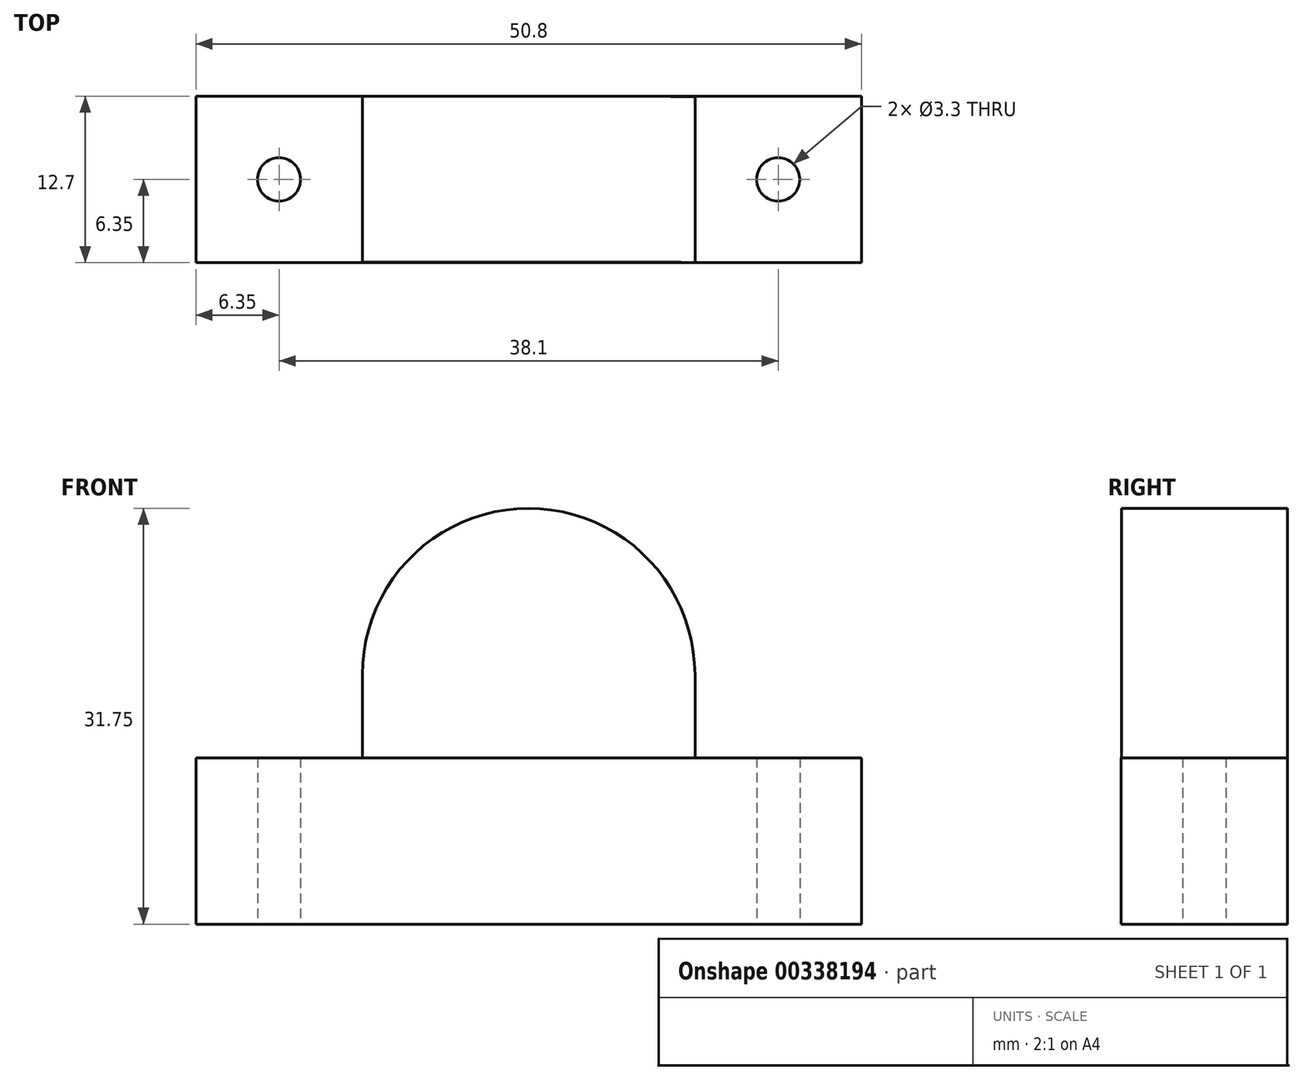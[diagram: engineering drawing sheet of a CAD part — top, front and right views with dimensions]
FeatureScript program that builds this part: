
annotation { "Feature Type Name" : "Feature", "Feature Type Description" : "" }
export const myFeature = defineFeature(function(context is Context, id is Id, definition is map)
    precondition{}
    {
        {
            var Q0;
            Q0=qCreatedBy(makeId("Top.planeOp"),FACE);
            var sketch = newSketch(context, id + "F0", { "sketchPlane" : qUnion([Q0])});
            skLineSegment(sketch, "E0.bottom", {"start": v(25.4, -6.35) * mm, "end": v(-25.4, -6.35) * mm});
            skLineSegment(sketch, "E0.top", {"start": v(25.4, 6.35) * mm, "end": v(-25.4, 6.35) * mm});
            skLineSegment(sketch, "E0.left", {"start": v(25.4, -6.35) * mm, "end": v(25.4, 6.35) * mm});
            skLineSegment(sketch, "E0.right", {"start": v(-25.4, -6.35) * mm, "end": v(-25.4, 6.35) * mm});
            skPoint(sketch, "E0.middle", {"position": v(0, 0) * mm});
            skCircle(sketch, "E1", {"center": v(19.05, 0) * mm, "radius": 1.65 * mm});
            skCircle(sketch, "E2", {"center": v(-19.05, 0) * mm, "radius": 1.65 * mm});
            skSolve(sketch);
        }
        {
            var Q0;
            Q0=makeQuery(id+"F0.imprint","IMPRINT",FACE,{"disambiguationData":[TD([[makeQuery(id+"F0.imprint","IMPRINT",EDGE,{"derivedFrom":sQuery(id+"F0.wireOp",EDGE,"E0.bottom")}),-1.0]])]});
            var sketch = newSketch(context, id + "F1", { "sketchPlane" : qUnion([Q0])});
            skLineSegment(sketch, "E3", {"start": v(12.7, 6.33) * mm, "end": v(12.7, -6.33) * mm});
            skLineSegment(sketch, "E4", {"start": v(-12.7, 6.43) * mm, "end": v(-12.7, -6.31) * mm});
            skLineSegment(sketch, "E5", {"start": v(-12.7, 6.43) * mm, "end": v(12.7, 6.33) * mm});
            skLineSegment(sketch, "E6", {"start": v(-12.7, -6.31) * mm, "end": v(12.7, -6.33) * mm});
            skSolve(sketch);
        }
        {
            var Q0;
            {var subQ1=sQuery(id+"F1.wireOp",EDGE,"E3");Q0=makeQuery(id+"F1.imprint","IMPRINT",FACE,{"disambiguationData":[TD([[makeQuery(id+"F1.imprint","IMPRINT",EDGE,{"derivedFrom":subQ1}),-1.0]])]});}
            extrude(context, id + "F2", {"entities" : qUnion([Q0]), "depth" : 31.75 * mm});
        }
        {
            var Q0;
            Q0=makeQuery(id+"F0.imprint","IMPRINT",FACE,{"disambiguationData":[TD([[makeQuery(id+"F0.imprint","IMPRINT",EDGE,{"derivedFrom":sQuery(id+"F0.wireOp",EDGE,"E0.bottom")}),-1.0]])]});
            extrude(context, id + "F3", {"entities" : qUnion([Q0]), "operationType" : NewBodyOperationType.ADD, "depth" : 12.7 * mm});
        }
        {
            var Q0;
            Q0=makeQuery(id+"F2.opExtrude","CAP_EDGE",EDGE,{"disambiguationData":[OSD([sQuery(id+"F1.wireOp",EDGE,"E4")])],"isStart":false});
            fillet(context, id + "F4", {"entities" : qUnion([Q0]), "radius" : 12.7 * mm, "tangentPropagation" : true, "allowEdgeOverflow" : false});
        }
        {
            var Q0;
            Q0=makeQuery(id+"F2.opExtrude","CAP_EDGE",EDGE,{"disambiguationData":[OSD([sQuery(id+"F1.wireOp",EDGE,"E3")])],"isStart":false});
            fillet(context, id + "F5", {"entities" : qUnion([Q0]), "radius" : 12.7 * mm, "tangentPropagation" : true, "allowEdgeOverflow" : false});
        }
    });
